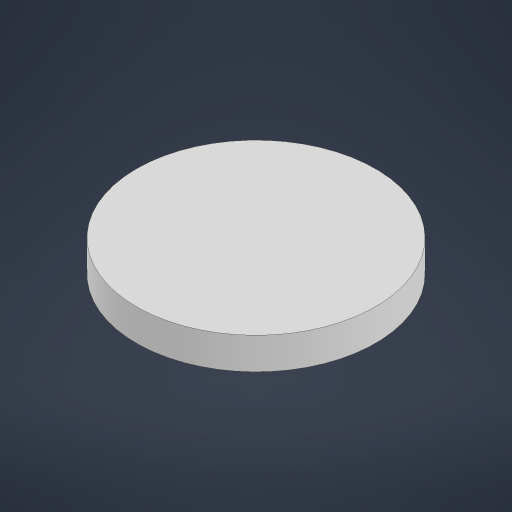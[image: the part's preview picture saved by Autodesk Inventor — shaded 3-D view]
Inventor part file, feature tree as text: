
AUTODESK INVENTOR PART (.ipt)
format: ipt  version: 2023 (Build 270158000, 158)  size: 152,064 bytes
history: native  units: mm
features: extrude x1, sketch x1
ambient origin geometry x8: Origin, YZ Plane, XZ Plane, XY Plane, X Axis, Y Axis, Z Axis, Center Point
bodies: Solid1 (feature_tree)
feature tree (2):
  extrude  "Extrusion1"  Depth=4.5mm TaperAngle=0.0deg
  sketch  "Sketch1"  dims[d0=34.0mm d1=4.5mm d2=0.0mm]
